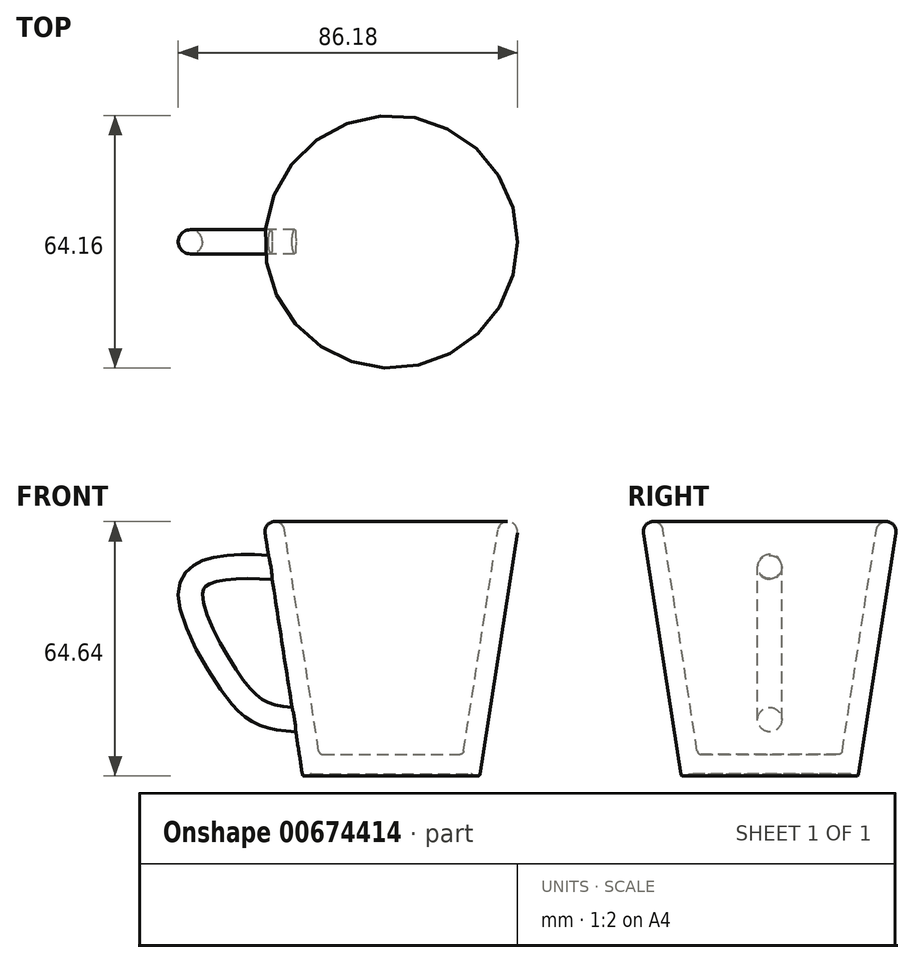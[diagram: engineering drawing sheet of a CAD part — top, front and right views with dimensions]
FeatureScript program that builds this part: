
annotation { "Feature Type Name" : "Feature", "Feature Type Description" : "" }
export const myFeature = defineFeature(function(context is Context, id is Id, definition is map)
    precondition{}
    {
        {
            var Q0;
            Q0=qCreatedBy(makeId("Front.planeOp"),FACE);
            var sketch = newSketch(context, id + "F0", { "sketchPlane" : qUnion([Q0])});
            skLineSegment(sketch, "E0", {"start": v(0, 0) * mm, "end": v(-20.5, 0) * mm});
            skLineSegment(sketch, "E1", {"start": v(-20.5, 0) * mm, "end": v(-21, -0.5) * mm});
            skLineSegment(sketch, "E2", {"start": v(-21, -0.5) * mm, "end": v(-22.5, -0.5) * mm});
            skLineSegment(sketch, "E3", {"start": v(-22.5, -0.5) * mm, "end": v(-32.5, 64.14) * mm});
            skLineSegment(sketch, "E4", {"start": v(-32.5, 64.14) * mm, "end": v(-27.44, 64.14) * mm});
            skLineSegment(sketch, "E5.0", {"start": v(-18.3, 5) * mm, "end": v(-27.44, 64.14) * mm});
            skLineSegment(sketch, "E6.0", {"start": v(0, 5) * mm, "end": v(-18.3, 5) * mm});
            skLineSegment(sketch, "E7", {"start": v(0, 5) * mm, "end": v(0, 0) * mm});
            skSolve(sketch);
        }
        {
            var Q0;
            Q0=qCreatedBy(makeId("Front.planeOp"),FACE);
            var sketch = newSketch(context, id + "F1", { "sketchPlane" : qUnion([Q0])});
            skLineSegment(sketch, "E8", {"start": v(0, 0) * mm, "end": v(0, 67.91) * mm, "construction": true});
            skSolve(sketch);
        }
        {
            var Q0;
            Q0 = qSketchRegion(id + "F0", true);
            var Q1;
            Q1=sQuery(id+"F1.wireOp",EDGE,"E8");
            revolve(context, id + "F2", {"entities" : qUnion([Q0]), "axis" : qUnion([Q1]), "revolveType" : RevolveType.FULL});
        }
        {
            var Q0;
            Q0=makeQuery(id+"F2.opRevolve","SWEPT_EDGE",EDGE,{"disambiguationData":[OSD([sQuery(id+"F0.wireOp",EDGE,"E2"),sQuery(id+"F0.wireOp",EDGE,"E3")])]});
            var Q1;
            Q1=makeQuery(id+"F2.opRevolve","SWEPT_EDGE",EDGE,{"disambiguationData":[OSD([sQuery(id+"F0.wireOp",EDGE,"E1"),sQuery(id+"F0.wireOp",EDGE,"E2")])]});
            var Q2;
            Q2=makeQuery(id+"F2.opRevolve","SWEPT_EDGE",EDGE,{"disambiguationData":[OSD([sQuery(id+"F0.wireOp",EDGE,"E0"),sQuery(id+"F0.wireOp",EDGE,"E1")])]});
            fillet(context, id + "F3", {"entities" : qUnion([Q0, Q1, Q2]), "radius" : .5 * mm, "tangentPropagation" : true, "allowEdgeOverflow" : false});
        }
        {
            var Q0;
            Q0=makeQuery(id+"F2.opRevolve","SWEPT_EDGE",EDGE,{"disambiguationData":[OSD([sQuery(id+"F0.wireOp",EDGE,"E3"),sQuery(id+"F0.wireOp",EDGE,"E4")])]});
            var Q1;
            Q1=makeQuery(id+"F2.opRevolve","SWEPT_EDGE",EDGE,{"disambiguationData":[OSD([sQuery(id+"F0.wireOp",EDGE,"E4"),sQuery(id+"F0.wireOp",EDGE,"E5.0")])]});
            fillet(context, id + "F4", {"entities" : qUnion([Q0, Q1]), "radius" : 2.5 * mm, "tangentPropagation" : true, "allowEdgeOverflow" : false});
        }
        {
            var Q0;
            Q0=makeQuery(id+"F2.opRevolve","SWEPT_EDGE",EDGE,{"disambiguationData":[OSD([sQuery(id+"F0.wireOp",EDGE,"E5.0"),sQuery(id+"F0.wireOp",EDGE,"E6.0")])]});
            fillet(context, id + "F5", {"entities" : qUnion([Q0]), "radius" : 1 * mm, "tangentPropagation" : true, "allowEdgeOverflow" : false});
        }
        {
            var Q0;
            Q0=qCreatedBy(makeId("Front.planeOp"),FACE);
            var sketch = newSketch(context, id + "F6", { "sketchPlane" : qUnion([Q0])});
            skFitSpline(sketch, "E9", {"points": [v(-28.08, 52.33) * mm, v(-44.63, 51.98) * mm, v(-50.95, 46.7) * mm, v(-41.76, 24.63) * mm, v(-32.68, 15.43) * mm, v(-22.45, 13.7) * mm], "startDerivative": vector(-81.9, 4.82) * mm, "endDerivative": vector(62.89, -3.46) * mm});
            skSolve(sketch);
        }
        {
            var Q0;
            Q0=qCreatedBy(makeId("Right.planeOp"),FACE);
            var Q1;
            Q1=sQuery(id+"F6.wireOp",VERTEX,"E9.0.internal");
            cPlane(context, id + "F7", {"entities" : qUnion([Q0, Q1]), "cplaneType" : CPlaneType.PLANE_POINT, "offset" : 25 * mm, "width" : 150 * mm, "height" : 150 * mm});
        }
        {
            var Q0;
            Q0=qCreatedBy(id+"F7.planeOp",FACE);
            var sketch = newSketch(context, id + "F8", { "sketchPlane" : qUnion([Q0])});
            skCircle(sketch, "E10", {"center": v(0, 52.34) * mm, "radius": 3.07 * mm});
            skSolve(sketch);
        }
        {
            var Q0;
            Q0 = qSketchRegion(id + "F8", true);
            var Q1;
            Q1=sQuery(id+"F6.wireOp",EDGE,"E9");
            sweep(context, id + "F9", {"operationType" : NewBodyOperationType.ADD, "profiles" : qUnion([Q0]), "path" : qUnion([Q1])});
        }
    });
